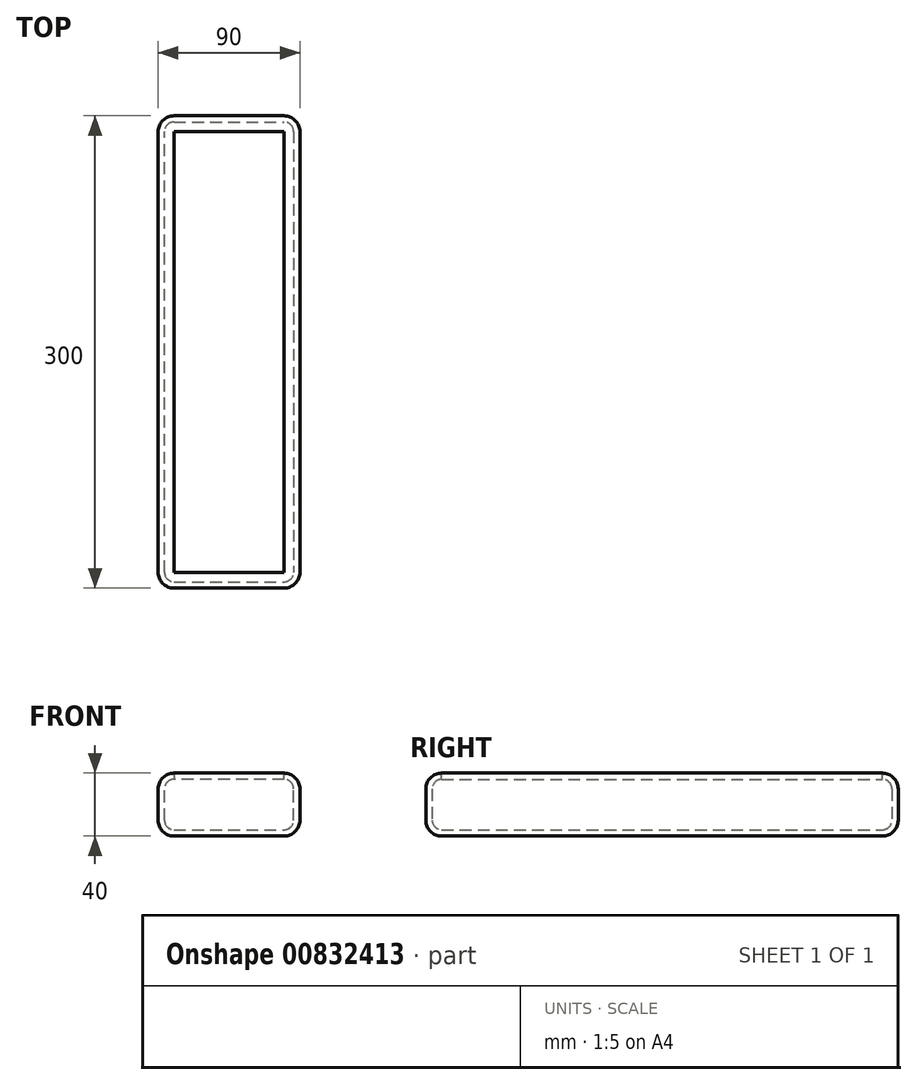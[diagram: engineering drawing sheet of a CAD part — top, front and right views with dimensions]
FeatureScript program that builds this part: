
annotation { "Feature Type Name" : "Feature", "Feature Type Description" : "" }
export const myFeature = defineFeature(function(context is Context, id is Id, definition is map)
    precondition{}
    {
        {
            var Q0;
            Q0=qCreatedBy(makeId("Top.planeOp"),FACE);
            var sketch = newSketch(context, id + "F0", { "sketchPlane" : qUnion([Q0])});
            skLineSegment(sketch, "E0.bottom", {"start": v(-123.4, -65.87) * mm, "end": v(-213.4, -65.87) * mm});
            skLineSegment(sketch, "E0.top", {"start": v(-123.4, 234.13) * mm, "end": v(-213.4, 234.13) * mm});
            skLineSegment(sketch, "E0.left", {"start": v(-123.4, -65.87) * mm, "end": v(-123.4, 234.13) * mm});
            skLineSegment(sketch, "E0.right", {"start": v(-213.4, -65.87) * mm, "end": v(-213.4, 234.13) * mm});
            skPoint(sketch, "E0.middle", {"position": v(-168.4, 84.13) * mm});
            skSolve(sketch);
        }
        {
            var Q0;
            Q0 = qSketchRegion(id + "F0", true);
            extrude(context, id + "F1", {"entities" : qUnion([Q0]), "depth" : 40 * mm, "offsetDistance" : 25 * mm});
        }
        {
            var Q0;
            Q0=makeQuery(id+"F1.opExtrude","CAP_EDGE",EDGE,{"disambiguationData":[OSD([sQuery(id+"F0.wireOp",EDGE,"E0.left")])],"isStart":false});
            var Q1;
            Q1=makeQuery(id+"F1.opExtrude","CAP_EDGE",EDGE,{"disambiguationData":[OSD([sQuery(id+"F0.wireOp",EDGE,"E0.bottom")])],"isStart":false});
            var Q2;
            Q2=makeQuery(id+"F1.opExtrude","CAP_EDGE",EDGE,{"disambiguationData":[OSD([sQuery(id+"F0.wireOp",EDGE,"E0.right")])],"isStart":false});
            var Q3;
            Q3=makeQuery(id+"F1.opExtrude","CAP_EDGE",EDGE,{"disambiguationData":[OSD([sQuery(id+"F0.wireOp",EDGE,"E0.top")])],"isStart":false});
            var Q4;
            Q4=makeQuery(id+"F1.opExtrude","CAP_EDGE",EDGE,{"disambiguationData":[OSD([sQuery(id+"F0.wireOp",EDGE,"E0.bottom")])],"isStart":true});
            var Q5;
            Q5=makeQuery(id+"F1.opExtrude","CAP_EDGE",EDGE,{"disambiguationData":[OSD([sQuery(id+"F0.wireOp",EDGE,"E0.left")])],"isStart":true});
            var Q6;
            Q6=makeQuery(id+"F1.opExtrude","SWEPT_EDGE",EDGE,{"disambiguationData":[OSD([sQuery(id+"F0.wireOp",EDGE,"E0.top"),sQuery(id+"F0.wireOp",EDGE,"E0.left")])]});
            var Q7;
            Q7=makeQuery(id+"F1.opExtrude","SWEPT_EDGE",EDGE,{"disambiguationData":[OSD([sQuery(id+"F0.wireOp",EDGE,"E0.bottom"),sQuery(id+"F0.wireOp",EDGE,"E0.left")])]});
            var Q8;
            Q8=makeQuery(id+"F1.opExtrude","SWEPT_EDGE",EDGE,{"disambiguationData":[OSD([sQuery(id+"F0.wireOp",EDGE,"E0.bottom"),sQuery(id+"F0.wireOp",EDGE,"E0.right")])]});
            var Q9;
            Q9=makeQuery(id+"F1.opExtrude","SWEPT_EDGE",EDGE,{"disambiguationData":[OSD([sQuery(id+"F0.wireOp",EDGE,"E0.top"),sQuery(id+"F0.wireOp",EDGE,"E0.right")])]});
            var Q10;
            Q10=makeQuery(id+"F1.opExtrude","CAP_EDGE",EDGE,{"disambiguationData":[OSD([sQuery(id+"F0.wireOp",EDGE,"E0.right")])],"isStart":true});
            var Q11;
            Q11=makeQuery(id+"F1.opExtrude","CAP_EDGE",EDGE,{"disambiguationData":[OSD([sQuery(id+"F0.wireOp",EDGE,"E0.top")])],"isStart":true});
            fillet(context, id + "F2", {"entities" : qUnion([Q0, Q1, Q2, Q3, Q4, Q5, Q6, Q7, Q8, Q9, Q10, Q11]), "radius" : 10 * mm, "tangentPropagation" : true, "allowEdgeOverflow" : false});
        }
        {
            var Q0;
            Q0=makeQuery(id+"F1.opExtrude","CAP_FACE",FACE,{"disambiguationData":[OSD([sQuery(id+"F0.wireOp",EDGE,"E0.bottom"),sQuery(id+"F0.wireOp",EDGE,"E0.top"),sQuery(id+"F0.wireOp",EDGE,"E0.left"),sQuery(id+"F0.wireOp",EDGE,"E0.right")])],"isStart":false});
            shell(context, id + "F3", {"entities" : qUnion([Q0]), "thickness" : 4 * mm});
        }
    });
